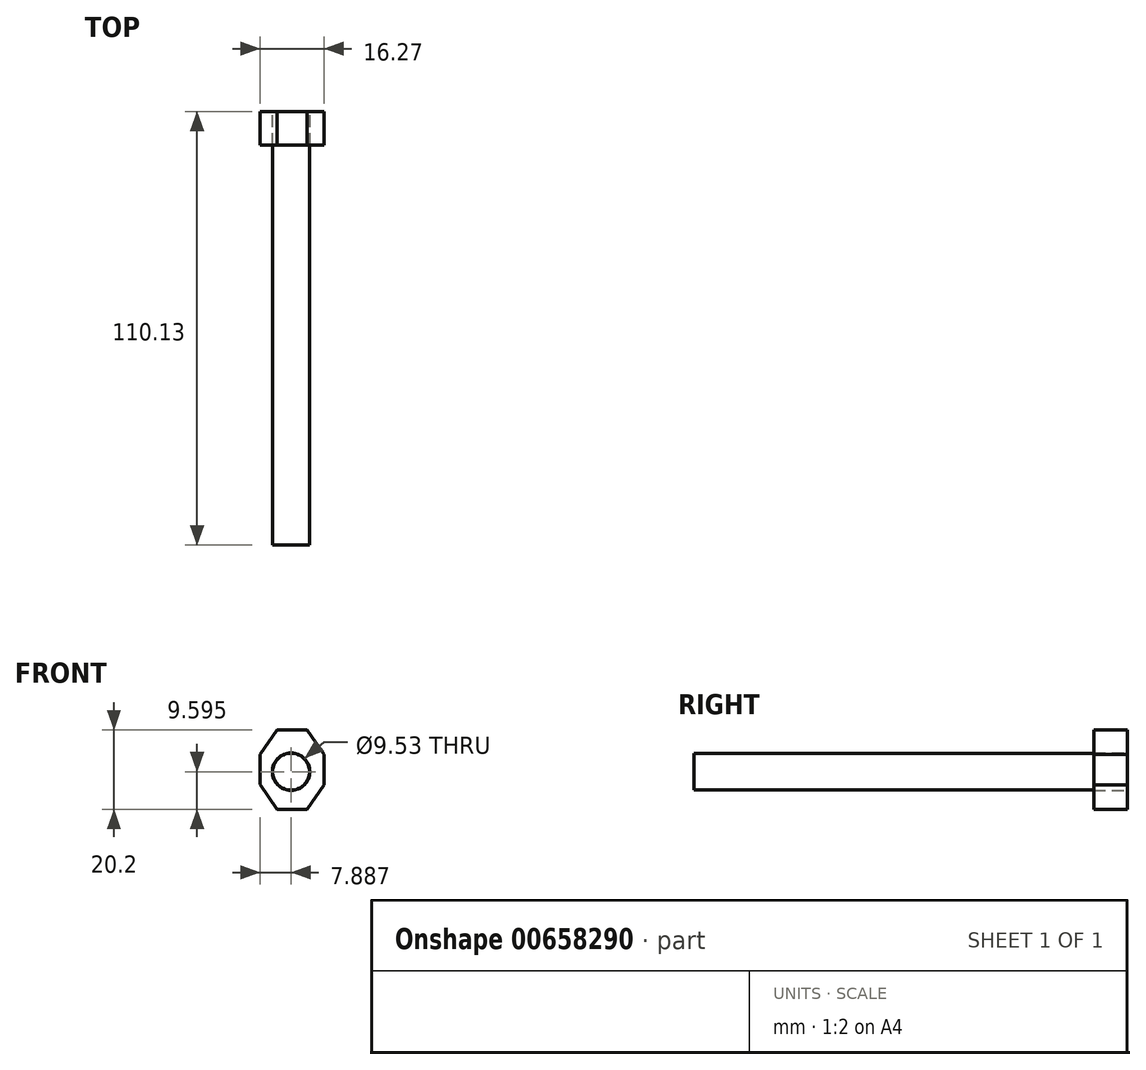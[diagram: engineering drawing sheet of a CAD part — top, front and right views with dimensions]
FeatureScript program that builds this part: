
annotation { "Feature Type Name" : "Feature", "Feature Type Description" : "" }
export const myFeature = defineFeature(function(context is Context, id is Id, definition is map)
    precondition{}
    {
        {
            var Q0;
            Q0=qCreatedBy(makeId("Front.planeOp"),FACE);
            var sketch = newSketch(context, id + "F0", { "sketchPlane" : qUnion([Q0])});
            skLineSegment(sketch, "E0", {"start": v(0, 0) * mm, "end": v(0, -7.62) * mm});
            skLineSegment(sketch, "E1", {"start": v(0, -7.62) * mm, "end": v(4.27, -13.93) * mm});
            skLineSegment(sketch, "E2", {"start": v(4.27, -13.93) * mm, "end": v(11.89, -13.93) * mm});
            skLineSegment(sketch, "E3", {"start": v(11.89, -13.93) * mm, "end": v(16.27, -7.7) * mm});
            skLineSegment(sketch, "E4", {"start": v(16.27, -7.7) * mm, "end": v(16.27, 0) * mm});
            skLineSegment(sketch, "E5", {"start": v(16.27, 0) * mm, "end": v(11.95, 6.27) * mm});
            skLineSegment(sketch, "E6", {"start": v(11.95, 6.27) * mm, "end": v(4.33, 6.27) * mm});
            skLineSegment(sketch, "E7", {"start": v(4.33, 6.27) * mm, "end": v(0, 0) * mm});
            skCircle(sketch, "E8", {"center": v(7.89, -4.34) * mm, "radius": 4.76 * mm});
            skSolve(sketch);
        }
        {
            var Q0;
            Q0 = qSketchRegion(id + "F0", true);
            extrude(context, id + "F1", {"entities" : qUnion([Q0]), "depth" : 8.53 * mm, "offsetDistance" : 25.4 * mm});
        }
        {
            var Q0;
            Q0=makeQuery(id+"F1.opExtrude","CAP_FACE",FACE,{"disambiguationData":[OSD([sQuery(id+"F0.wireOp",EDGE,"E0"),sQuery(id+"F0.wireOp",EDGE,"E1"),sQuery(id+"F0.wireOp",EDGE,"E2"),sQuery(id+"F0.wireOp",EDGE,"E3"),sQuery(id+"F0.wireOp",EDGE,"E4"),sQuery(id+"F0.wireOp",EDGE,"E5"),sQuery(id+"F0.wireOp",EDGE,"E6"),sQuery(id+"F0.wireOp",EDGE,"E7"),sQuery(id+"F0.wireOp",EDGE,"E8")])],"isStart":false});
            var sketch = newSketch(context, id + "F2", { "sketchPlane" : qUnion([Q0])});
            skCircle(sketch, "E9", {"center": v(7.89, -4.34) * mm, "radius": 4.68 * mm});
            skSolve(sketch);
        }
        {
            var Q0;
            Q0 = qSketchRegion(id + "F2", true);
            extrude(context, id + "F3", {"entities" : qUnion([Q0]), "depth" : 101.6 * mm, "offsetDistance" : 25.4 * mm});
        }
    });
